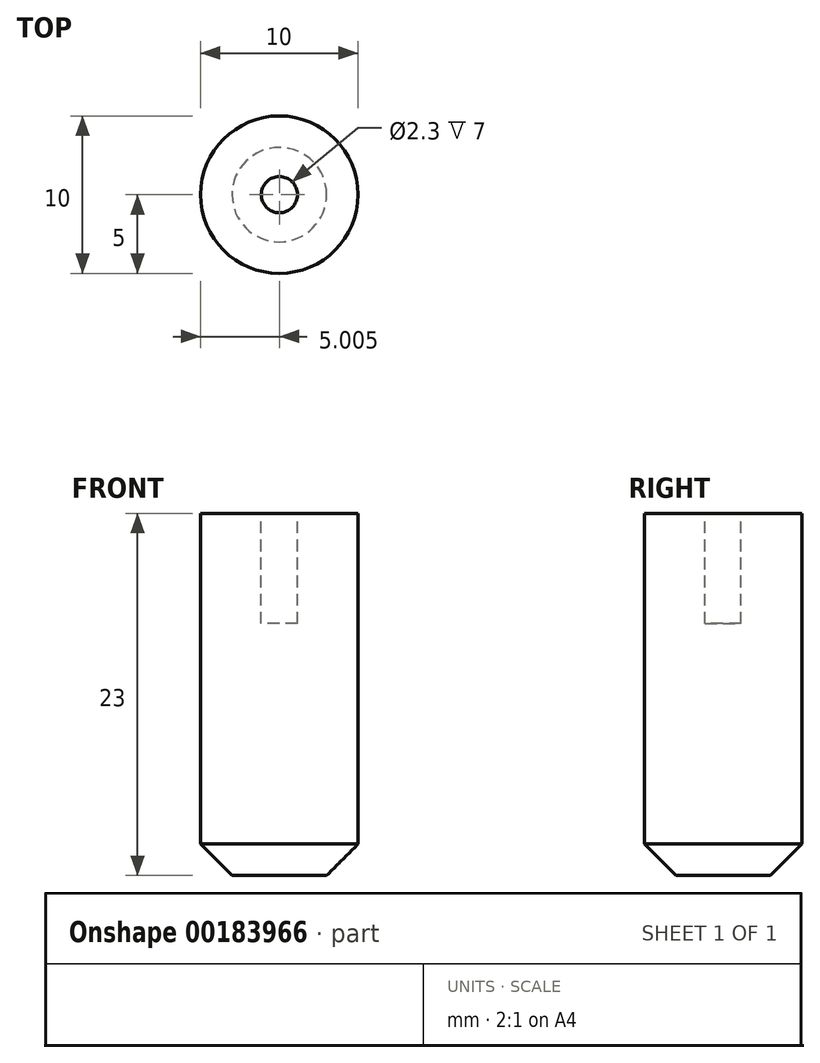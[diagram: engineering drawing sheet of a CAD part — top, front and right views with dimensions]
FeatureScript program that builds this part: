
annotation { "Feature Type Name" : "Feature", "Feature Type Description" : "" }
export const myFeature = defineFeature(function(context is Context, id is Id, definition is map)
    precondition{}
    {
        {
            var Q0;
            Q0=qCreatedBy(makeId("Top.planeOp"),FACE);
            var sketch = newSketch(context, id + "F0", { "sketchPlane" : qUnion([Q0])});
            skCircle(sketch, "E0", {"center": v(-44.12, 43.27) * mm, "radius": 5 * mm});
            skCircle(sketch, "E1", {"center": v(-44.12, 43.27) * mm, "radius": 2.5 * mm});
            skSolve(sketch);
        }
        {
            var Q0;
            Q0=makeQuery(id+"F0.imprint","IMPRINT",FACE,{"disambiguationData":[TD([[makeQuery(id+"F0.imprint","IMPRINT",EDGE,{"derivedFrom":sQuery(id+"F0.wireOp",EDGE,"E0")}),1.0]])]});
            var Q1;
            Q1=makeQuery(id+"F0.imprint","IMPRINT",FACE,{"disambiguationData":[TD([[makeQuery(id+"F0.imprint","IMPRINT",EDGE,{"derivedFrom":sQuery(id+"F0.wireOp",EDGE,"E1")}),1.0]])]});
            extrude(context, id + "F1", {"entities" : qUnion([Q0, Q1]), "depth" : 23 * mm});
        }
        {
            var Q0;
            Q0=makeQuery(id+"F1.opExtrude","CAP_FACE",FACE,{"disambiguationData":[OSD([sQuery(id+"F0.wireOp",EDGE,"E0")])],"isStart":false});
            var sketch = newSketch(context, id + "F2", { "sketchPlane" : qUnion([Q0])});
            skCircle(sketch, "E2", {"center": v(-44.12, 43.27) * mm, "radius": 1.15 * mm});
            skSolve(sketch);
        }
        {
            var Q0;
            Q0=makeQuery(id+"F2.imprint","IMPRINT",FACE,{"disambiguationData":[TD([[makeQuery(id+"F2.imprint","IMPRINT",EDGE,{"derivedFrom":sQuery(id+"F2.wireOp",EDGE,"E2")}),1.0]])]});
            var Q1;
            Q1=sQuery(id+"F2.wireOp",EDGE,"E2");
            extrude(context, id + "F3", {"entities" : qUnion([Q0]), "operationType" : NewBodyOperationType.REMOVE, "surfaceEntities" : qUnion([Q1]), "oppositeDirection" : true, "depth" : 7 * mm});
        }
        {
            var Q0;
            Q0=makeQuery(id+"F1.opExtrude","CAP_EDGE",EDGE,{"disambiguationData":[OSD([sQuery(id+"F0.wireOp",EDGE,"E0")])],"isStart":true});
            chamfer(context, id + "F4", {"entities" : qUnion([Q0]), "width" : 2 * mm, "tangentPropagation" : true});
        }
    });
